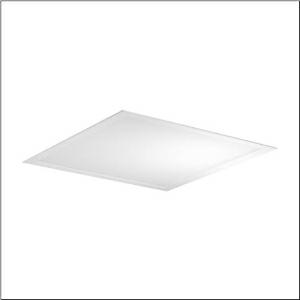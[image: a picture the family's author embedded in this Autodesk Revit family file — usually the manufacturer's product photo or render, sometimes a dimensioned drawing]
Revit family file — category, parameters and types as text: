
# Revit family: apollon_21_square_51mq11wd2454
name_source: partatom
category: Lighting Fixtures
units: mm (PartAtom-declared; Revit-internal decimal feet)

## family parameters
Cut with Voids When Loaded = No
Host = Face
Light Source = No
Part Type = Normal
Room Calculation Point = No
Round Connector Dimension = Use Diameter
Shared = No

## types (1)
- Apollon 21 square (1 x LED, 4200 lm, 24.7 W, 4000K)
    Apparent Load = 25 VA
    CIE Flux Codes = 60 87 97 100 100
    Color Rendering = 80
    Color Temperature = 4000K
    Default Elevation = 1800 mm
    Description = Apollon 21 square, office luminaire, primary optical cover: micro prismatic cover, of PMMA, CAT 2 (L<= 3000cd/m²), light emission: direct distribution, primary light characteristic: symmetric, installation type: lay-in mounting, recessed, LED, rated luminous flux: 4.200lm, luminous efficacy: 170lm/W, light colour: 840, colour temperature: 4000K, control gear: DALI 2, Multilumen, with terminal, 5-pole, mains connection: 220..240V, AC/DC, 0/50..60Hz, rated input power: 24.7W, suitable for self-contained emergency lighting element 59MQE002602A with integrated self-test function according to EN 60598-2-22, housing, of aluminium, coated, traffic white (RAL 9016), module: M625, length: 620mm, width: 620mm, height: 55mm, housing upper side, of sheet steel, galvanised, protection rating (complete): IP20, protection rating (lamp compartment, on room side): IP54, insulation class (complete): insulation class II (safety insulation), certification: CE, ENEC, UKCA, impact resistance: IK03, permissible operating ambient temperature: -20..+45°C, standard: EN 60598-2-22, corresponds to IFS (International Featured Standards) requirements for safety and quality in the food industry, packaging unit: 1 piece
    Height = 0 mm  [stored 0 ft]
    Lamp = 1 x LED
    Lamp Light Flux = 4200 lm
    Lamp Power = 24.7 W
    Lamp count = 1
    Length = 620 mm
    Luminous efficacy = 170 lm/W
    Manufacturer = Siteco
    ModVariant = No
    Model = 51MQ11WD2454
    Mounting Place = Ceiling
    Mounting Type = Recessed
    Number of Poles = 1
    OnlyDefault = Yes
    Power Factor = 1
    Product Name = Apollon 21 square
    Product group = office luminaire | ceiling recessed
    ProductGroupID = 400
    Protection Class = Protection class II
    Protection Degree = IP 20
    RLX_Detail_Level = 1
    RLX_Emergency_Light_Flux = 0 lm
    RLX_Emergency_Type = 0
    RLX_Emergency_Type_DB = No
    RlxData = <blob elided: 13293 chars, md5=efa09d9f>
    Socket = socket
    Standby Power = 0 W
    System Light Flux = 4200 lm
    System Power = 25 W
    Type Comments = Product without accessories
    Type Image = l_1291054.jpg
    URL = http://relux.com
    VarID = ---
    Voltage = 0 V
    Weight = 0.00 kg
    Width = 620 mm

note: [stored X ft] marks values corroborated as IEEE doubles in the binary element streams (Revit-internal decimal feet)

## geometry (parser evidence)
native form markers: Sweep x12
no freeform markers — native parametric forms only
